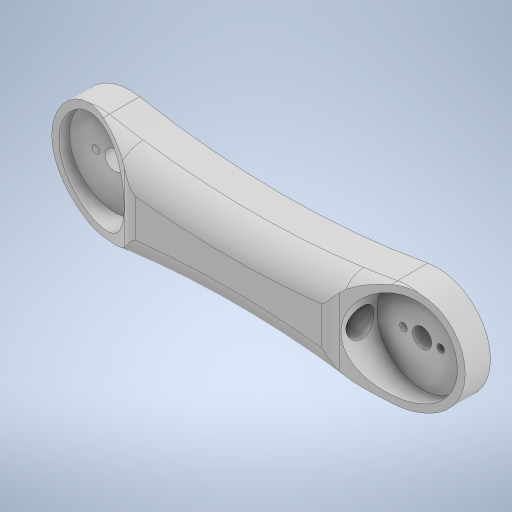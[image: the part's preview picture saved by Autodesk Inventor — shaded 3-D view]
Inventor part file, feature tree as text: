
AUTODESK INVENTOR PART (.ipt)
format: ipt  version: 2024.1 (Build 281209000, 209)  size: 371,712 bytes
history: native  units: in
note: dims shown in document units (in); Inventor stores cm internally (conversion verified against a paired STEP export)
features: extrude x4, sketch x4, fillet x2
ambient origin geometry x8: Origin, YZ Plane, XZ Plane, XY Plane, X Axis, Y Axis, Z Axis, Center Point
bodies: Solid1 (feature_tree)
feature tree (10):
  extrude  "Extrusion1"  Depth=4.1339in
  sketch  "Sketch2"  dims[d2=12.0079in d3=0.5906in d4=0.5906in]
  extrude  "Extrusion3"  Depth=0.5906in
  fillet  "Fillet3"  Radius=0.5906in
  extrude  "Extrusion4"  Depth=0.748in
  fillet  "Fillet4"  Radius=0.2992in
  extrude  "Extrusion5"  Depth=1.2598in
  sketch  "Sketch1"  dims[d0=4.1339in d1=4.1339in]
  sketch  "Sketch3"  dims[d5=0.748in d6=0.748in d7=0.2992in]
  sketch  "Sketch4"  dims[d8=0.2992in d9=0.2992in d10=0.2992in d11=0.7283in d12=0.7283in d13=0.7283in d14=0.7283in d15=2.1654in d16=0.0in d18=0.9843in d19=4.1339in d20=0.3937in d24=3.5433in d25=12.0079in d26=3.5433in d27=1.5669in d28=0.0in d29=0.9843in d30=0.0in d31=0.0in d32=1.1811in d33=1.1024in d34=1.2598in d35=0.0in d36=0.0in]
